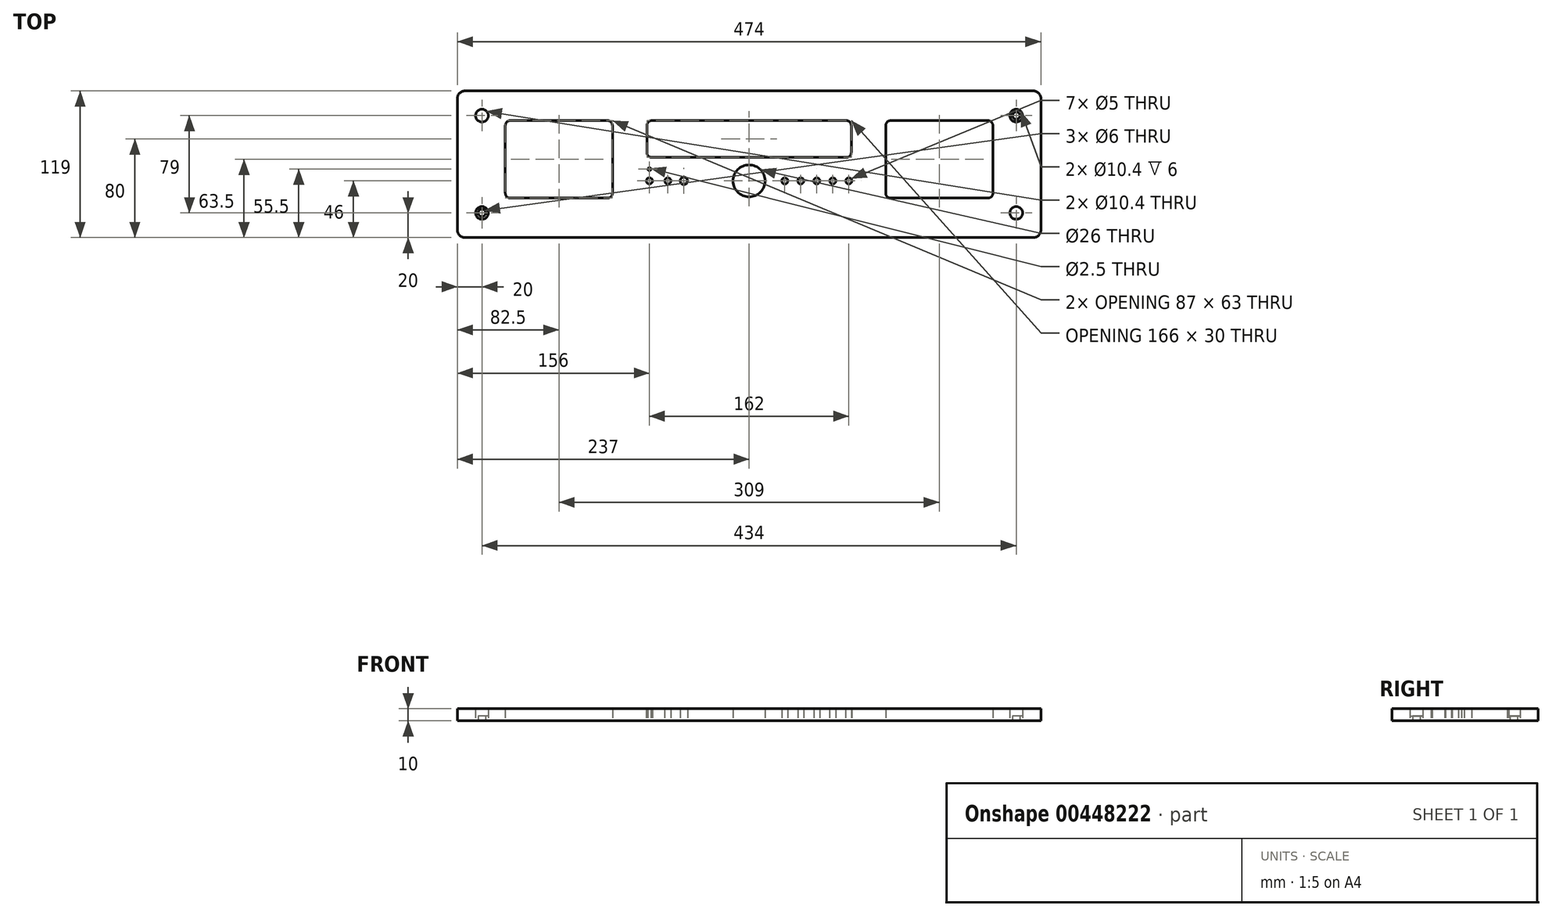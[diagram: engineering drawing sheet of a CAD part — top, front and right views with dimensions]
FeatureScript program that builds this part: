
annotation { "Feature Type Name" : "Feature", "Feature Type Description" : "" }
export const myFeature = defineFeature(function(context is Context, id is Id, definition is map)
    precondition{}
    {
        {
            var Q0;
            Q0=qCreatedBy(makeId("Top.planeOp"),FACE);
            var sketch = newSketch(context, id + "F0", { "sketchPlane" : qUnion([Q0])});
            skLineSegment(sketch, "E0.bottom", {"start": v(231, -59.5) * mm, "end": v(-231, -59.5) * mm});
            skLineSegment(sketch, "E0.top", {"start": v(231, 59.5) * mm, "end": v(-231, 59.5) * mm});
            skLineSegment(sketch, "E0.left", {"start": v(237, -53.5) * mm, "end": v(237, 53.5) * mm});
            skLineSegment(sketch, "E0.right", {"start": v(-237, -53.5) * mm, "end": v(-237, 53.5) * mm});
            skPoint(sketch, "E0.middle", {"position": v(0, 0) * mm});
            skPoint(sketch, "E1.visualSharp", {"position": v(-237, 59.5) * mm});
            skArc(sketch, "E1.filletArc", {"start": v(-231, 59.5) * mm, "mid": v(-235.24, 57.74) * mm, "end": v(-237, 53.5) * mm});
            skPoint(sketch, "E2.visualSharp", {"position": v(237, 59.5) * mm});
            skArc(sketch, "E2.filletArc", {"start": v(237, 53.5) * mm, "mid": v(235.24, 57.74) * mm, "end": v(231, 59.5) * mm});
            skPoint(sketch, "E3.visualSharp", {"position": v(237, -59.5) * mm});
            skArc(sketch, "E3.filletArc", {"start": v(231, -59.5) * mm, "mid": v(235.24, -57.74) * mm, "end": v(237, -53.5) * mm});
            skPoint(sketch, "E4.visualSharp", {"position": v(-237, -59.5) * mm});
            skArc(sketch, "E4.filletArc", {"start": v(-237, -53.5) * mm, "mid": v(-235.24, -57.74) * mm, "end": v(-231, -59.5) * mm});
            skLineSegment(sketch, "E5.bottom", {"start": v(-194, 35.5) * mm, "end": v(-115, 35.5) * mm});
            skLineSegment(sketch, "E5.top", {"start": v(-194, -27.5) * mm, "end": v(-115, -27.5) * mm});
            skLineSegment(sketch, "E5.left", {"start": v(-198, 31.5) * mm, "end": v(-198, -23.5) * mm});
            skLineSegment(sketch, "E5.right", {"start": v(-111, 31.5) * mm, "end": v(-111, -23.5) * mm});
            skLineSegment(sketch, "E6", {"start": v(0, 69.77) * mm, "end": v(0, -114.1) * mm, "construction": true});
            skPoint(sketch, "E6.endSnap0", {"position": v(0, -59.5) * mm});
            skLineSegment(sketch, "E7.MirrorCS", {"start": v(111, 31.5) * mm, "end": v(111, -23.5) * mm});
            skLineSegment(sketch, "E8.MirrorCS", {"start": v(198, 31.5) * mm, "end": v(198, -23.5) * mm});
            skLineSegment(sketch, "E9.MirrorCS", {"start": v(194, 35.5) * mm, "end": v(115, 35.5) * mm});
            skLineSegment(sketch, "E10.MirrorCS", {"start": v(194, -27.5) * mm, "end": v(115, -27.5) * mm});
            skLineSegment(sketch, "E11.bottom", {"start": v(79, 35.5) * mm, "end": v(-79, 35.5) * mm});
            skLineSegment(sketch, "E11.top", {"start": v(79, 5.5) * mm, "end": v(-79, 5.5) * mm});
            skLineSegment(sketch, "E11.left", {"start": v(83, 31.5) * mm, "end": v(83, 9.5) * mm});
            skLineSegment(sketch, "E11.right", {"start": v(-83, 31.5) * mm, "end": v(-83, 9.5) * mm});
            skPoint(sketch, "E12.visualSharp", {"position": v(-198, 35.5) * mm});
            skArc(sketch, "E12.filletArc", {"start": v(-194, 35.5) * mm, "mid": v(-196.83, 34.33) * mm, "end": v(-198, 31.5) * mm});
            skPoint(sketch, "E13.visualSharp", {"position": v(-111, 35.5) * mm});
            skArc(sketch, "E13.filletArc", {"start": v(-111, 31.5) * mm, "mid": v(-112.17, 34.33) * mm, "end": v(-115, 35.5) * mm});
            skPoint(sketch, "E14.visualSharp", {"position": v(-111, -27.5) * mm});
            skArc(sketch, "E14.filletArc", {"start": v(-115, -27.5) * mm, "mid": v(-112.17, -26.33) * mm, "end": v(-111, -23.5) * mm});
            skPoint(sketch, "E15.visualSharp", {"position": v(-198, -27.5) * mm});
            skArc(sketch, "E15.filletArc", {"start": v(-198, -23.5) * mm, "mid": v(-196.83, -26.33) * mm, "end": v(-194, -27.5) * mm});
            skPoint(sketch, "E16.visualSharp", {"position": v(-83, 5.5) * mm});
            skArc(sketch, "E16.filletArc", {"start": v(-83, 9.5) * mm, "mid": v(-81.83, 6.67) * mm, "end": v(-79, 5.5) * mm});
            skPoint(sketch, "E17.visualSharp", {"position": v(-83, 35.5) * mm});
            skArc(sketch, "E17.filletArc", {"start": v(-79, 35.5) * mm, "mid": v(-81.83, 34.33) * mm, "end": v(-83, 31.5) * mm});
            skPoint(sketch, "E18.visualSharp", {"position": v(83, 35.5) * mm});
            skArc(sketch, "E18.filletArc", {"start": v(83, 31.5) * mm, "mid": v(81.83, 34.33) * mm, "end": v(79, 35.5) * mm});
            skPoint(sketch, "E19.visualSharp", {"position": v(83, 5.5) * mm});
            skArc(sketch, "E19.filletArc", {"start": v(79, 5.5) * mm, "mid": v(81.83, 6.67) * mm, "end": v(83, 9.5) * mm});
            skPoint(sketch, "E20.visualSharp", {"position": v(111, 35.5) * mm});
            skArc(sketch, "E20.filletArc", {"start": v(115, 35.5) * mm, "mid": v(112.17, 34.33) * mm, "end": v(111, 31.5) * mm});
            skPoint(sketch, "E21.visualSharp", {"position": v(198, 35.5) * mm});
            skArc(sketch, "E21.filletArc", {"start": v(198, 31.5) * mm, "mid": v(196.83, 34.33) * mm, "end": v(194, 35.5) * mm});
            skPoint(sketch, "E22.visualSharp", {"position": v(198, -27.5) * mm});
            skArc(sketch, "E22.filletArc", {"start": v(194, -27.5) * mm, "mid": v(196.83, -26.33) * mm, "end": v(198, -23.5) * mm});
            skPoint(sketch, "E23.visualSharp", {"position": v(111, -27.5) * mm});
            skArc(sketch, "E23.filletArc", {"start": v(111, -23.5) * mm, "mid": v(112.17, -26.33) * mm, "end": v(115, -27.5) * mm});
            skCircle(sketch, "E24", {"center": v(-217, -39.5) * mm, "radius": 3 * mm});
            skCircle(sketch, "E25", {"center": v(-217, -39.5) * mm, "radius": 5.2 * mm});
            skLineSegment(sketch, "E26", {"start": v(71.63, 0) * mm, "end": v(-74.64, 0) * mm, "construction": true});
            skCircle(sketch, "E27.MirrorC", {"center": v(-217, 39.5) * mm, "radius": 5.2 * mm});
            skCircle(sketch, "E28.MirrorC", {"center": v(-217, 39.5) * mm, "radius": 3 * mm});
            skCircle(sketch, "E29.MirrorC", {"center": v(217, -39.5) * mm, "radius": 3 * mm});
            skCircle(sketch, "E30.MirrorC", {"center": v(217, -39.5) * mm, "radius": 5.2 * mm});
            skCircle(sketch, "E31.MirrorC", {"center": v(217, 39.5) * mm, "radius": 3 * mm});
            skCircle(sketch, "E32.MirrorC", {"center": v(217, 39.5) * mm, "radius": 5.2 * mm});
            skLineSegment(sketch, "E33", {"start": v(-83, -13.5) * mm, "end": v(83, -13.5) * mm, "construction": true});
            skCircle(sketch, "E34", {"center": v(0, -13.5) * mm, "radius": 13 * mm});
            skCircle(sketch, "E35", {"center": v(-81, -13.5) * mm, "radius": 2.5 * mm});
            skCircle(sketch, "E36", {"center": v(-66, -13.5) * mm, "radius": 2.5 * mm});
            skCircle(sketch, "E37", {"center": v(-53, -13.5) * mm, "radius": 3 * mm});
            skCircle(sketch, "E38", {"center": v(29, -13.5) * mm, "radius": 2.5 * mm});
            skCircle(sketch, "E39", {"center": v(42, -13.5) * mm, "radius": 2.5 * mm});
            skCircle(sketch, "E40", {"center": v(55, -13.5) * mm, "radius": 2.5 * mm});
            skCircle(sketch, "E41", {"center": v(68, -13.5) * mm, "radius": 2.5 * mm});
            skCircle(sketch, "E42", {"center": v(81, -13.5) * mm, "radius": 2.5 * mm});
            skCircle(sketch, "E43", {"center": v(-81, -4) * mm, "radius": 1.25 * mm});
            skSolve(sketch);
        }
        {
            var Q0;
            Q0=makeQuery(id+"F0.imprint","IMPRINT",FACE,{"disambiguationData":[TD([[makeQuery(id+"F0.imprint","IMPRINT",EDGE,{"derivedFrom":sQuery(id+"F0.wireOp",EDGE,"E0.bottom")}),-1.0]])]});
            extrude(context, id + "F1", {"entities" : qUnion([Q0]), "depth" : 10 * mm});
        }
        {
            var Q0;
            Q0=makeQuery(id+"F0.imprint","IMPRINT",FACE,{"disambiguationData":[TD([[makeQuery(id+"F0.imprint","IMPRINT",EDGE,{"derivedFrom":sQuery(id+"F0.wireOp",EDGE,"E27.MirrorC")}),-1.0]])]});
            var Q1;
            Q1=makeQuery(id+"F0.imprint","IMPRINT",FACE,{"disambiguationData":[TD([[makeQuery(id+"F0.imprint","IMPRINT",EDGE,{"derivedFrom":sQuery(id+"F0.wireOp",EDGE,"E24")}),-1.0]])]});
            var Q2;
            Q2=makeQuery(id+"F0.imprint","IMPRINT",FACE,{"disambiguationData":[TD([[makeQuery(id+"F0.imprint","IMPRINT",EDGE,{"derivedFrom":sQuery(id+"F0.wireOp",EDGE,"E30.MirrorC")}),-1.0]])]});
            var Q3;
            Q3=makeQuery(id+"F0.imprint","IMPRINT",FACE,{"disambiguationData":[TD([[makeQuery(id+"F0.imprint","IMPRINT",EDGE,{"derivedFrom":sQuery(id+"F0.wireOp",EDGE,"E31.MirrorC")}),-1.0]])]});
            extrude(context, id + "F2", {"entities" : qUnion([Q0, Q1, Q2, Q3]), "operationType" : NewBodyOperationType.ADD, "depth" : 4 * mm});
        }
    });
